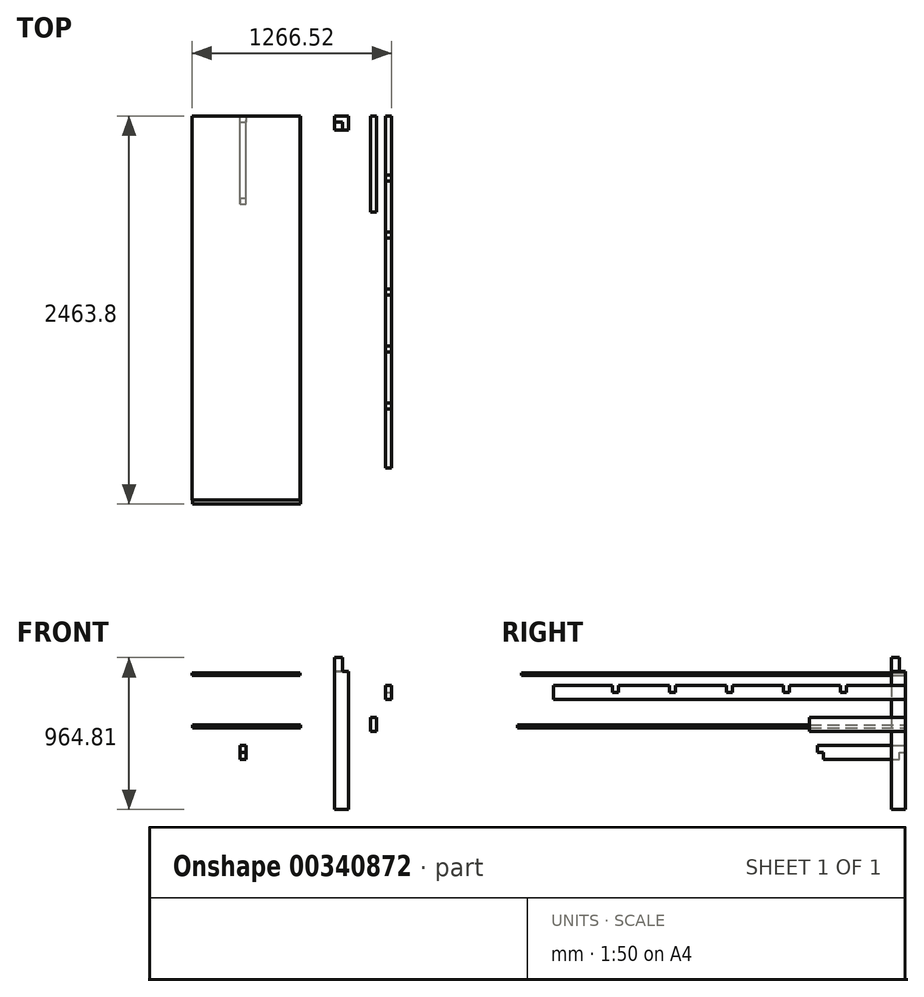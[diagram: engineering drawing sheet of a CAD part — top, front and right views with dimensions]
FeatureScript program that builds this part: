
annotation { "Feature Type Name" : "Feature", "Feature Type Description" : "" }
export const myFeature = defineFeature(function(context is Context, id is Id, definition is map)
    precondition{}
    {
        {
            var Q0;
            Q0=qCreatedBy(makeId("Front.planeOp"),FACE);
            var sketch = newSketch(context, id + "F0", { "sketchPlane" : qUnion([Q0])});
            skLineSegment(sketch, "E0.bottom", {"start": v(-17.05, 357.24) * mm, "end": v(-55.15, 357.24) * mm});
            skLineSegment(sketch, "E0.top", {"start": v(-17.05, -518.67) * mm, "end": v(-105.95, -518.67) * mm});
            skLineSegment(sketch, "E0.left", {"start": v(-17.05, 357.24) * mm, "end": v(-17.05, -518.67) * mm});
            skLineSegment(sketch, "E1", {"start": v(-105.95, -518.67) * mm, "end": v(-105.95, 446.14) * mm});
            skLineSegment(sketch, "E2", {"start": v(-105.95, 446.14) * mm, "end": v(-55.15, 446.14) * mm});
            skLineSegment(sketch, "E3", {"start": v(-55.15, 446.14) * mm, "end": v(-55.15, 357.24) * mm});
            skPoint(sketch, "E4.orphan", {"position": v(-105.95, 357.24) * mm});
            skLineSegment(sketch, "E5", {"start": v(-105.95, -518.67) * mm, "end": v(-105.95, 805.3) * mm, "construction": true});
            skPoint(sketch, "E6", {"position": v(-105.95, 805.3) * mm});
            skPoint(sketch, "E7", {"position": v(-105.95, 737.04) * mm});
            skPoint(sketch, "E8", {"position": v(-105.95, 678.3) * mm});
            skPoint(sketch, "E9", {"position": v(-105.95, 605.28) * mm});
            skPoint(sketch, "E10", {"position": v(-105.95, 464) * mm});
            skPoint(sketch, "E11", {"position": v(-105.95, 483.04) * mm});
            skSolve(sketch);
        }
        {
            var Q0;
            Q0=makeQuery(id+"F0.imprint","IMPRINT",FACE,{"disambiguationData":[TD([[makeQuery(id+"F0.imprint","IMPRINT",EDGE,{"derivedFrom":sQuery(id+"F0.wireOp",EDGE,"E0.bottom")}),1.0]])]});
            extrude(context, id + "F1", {"entities" : qUnion([Q0]), "depth" : 88.9 * mm, "offsetDistance" : 25.4 * mm});
        }
        {
            var Q0;
            Q0=makeQuery(id+"F1.opExtrude","SWEPT_FACE",FACE,{"disambiguationData":[OSD([sQuery(id+"F0.wireOp",EDGE,"E3")])]});
            var sketch = newSketch(context, id + "F2", { "sketchPlane" : qUnion([Q0])});
            skLineSegment(sketch, "E12.bottom", {"start": v(0, 446.14) * mm, "end": v(-38.1, 446.14) * mm});
            skLineSegment(sketch, "E12.top", {"start": v(0, 357.24) * mm, "end": v(-38.1, 357.24) * mm});
            skLineSegment(sketch, "E12.left", {"start": v(0, 446.14) * mm, "end": v(0, 357.24) * mm});
            skLineSegment(sketch, "E12.right", {"start": v(-38.1, 446.14) * mm, "end": v(-38.1, 357.24) * mm});
            skSolve(sketch);
        }
        {
            var Q0;
            Q0=makeQuery(id+"F2.imprint","IMPRINT",FACE,{"disambiguationData":[TD([[makeQuery(id+"F2.imprint","IMPRINT",EDGE,{"derivedFrom":sQuery(id+"F2.wireOp",EDGE,"E12.bottom")}),-1.0]])]});
            var Q1;
            Q1=makeQuery(id+"F1.opExtrude","SWEPT_FACE",FACE,{"disambiguationData":[OSD([sQuery(id+"F0.wireOp",EDGE,"E1")])]});
            extrude(context, id + "F3", {"entities" : qUnion([Q0]), "operationType" : NewBodyOperationType.REMOVE, "endBound" : BoundingType.UP_TO_SURFACE, "oppositeDirection" : true, "depth" : 25.4 * mm, "endBoundEntityFace" : qUnion([Q1]), "offsetDistance" : 25.4 * mm});
        }
        {
            var Q0;
            Q0=qCreatedBy(makeId("Front.planeOp"),FACE);
            var sketch = newSketch(context, id + "F4", { "sketchPlane" : qUnion([Q0])});
            skLineSegment(sketch, "E13.bottom", {"start": v(217.3, 269.52) * mm, "end": v(255.4, 269.52) * mm});
            skLineSegment(sketch, "E13.top", {"start": v(217.3, 180.62) * mm, "end": v(255.4, 180.62) * mm});
            skLineSegment(sketch, "E13.left", {"start": v(217.3, 269.52) * mm, "end": v(217.3, 180.62) * mm});
            skLineSegment(sketch, "E13.right", {"start": v(255.4, 269.52) * mm, "end": v(255.4, 180.62) * mm});
            skSolve(sketch);
        }
        {
            var Q0;
            Q0=makeQuery(id+"F4.imprint","IMPRINT",FACE,{"disambiguationData":[TD([[makeQuery(id+"F4.imprint","IMPRINT",EDGE,{"derivedFrom":sQuery(id+"F4.wireOp",EDGE,"E13.bottom")}),-1.0]])]});
            extrude(context, id + "F5", {"entities" : qUnion([Q0]), "depth" : 2235.2 * mm, "offsetDistance" : 25.4 * mm});
        }
        {
            var Q0;
            Q0=makeQuery(id+"F5.opExtrude","SWEPT_FACE",FACE,{"disambiguationData":[OSD([sQuery(id+"F4.wireOp",EDGE,"E13.right")])]});
            var sketch = newSketch(context, id + "F6", { "sketchPlane" : qUnion([Q0])});
            skLineSegment(sketch, "E14.bottom", {"start": v(-1136.65, 269.52) * mm, "end": v(-1098.55, 269.52) * mm});
            skLineSegment(sketch, "E14.top", {"start": v(-1136.65, 225.07) * mm, "end": v(-1098.55, 225.07) * mm});
            skLineSegment(sketch, "E14.left", {"start": v(-1136.65, 269.52) * mm, "end": v(-1136.65, 225.07) * mm});
            skLineSegment(sketch, "E14.right", {"start": v(-1098.55, 269.52) * mm, "end": v(-1098.55, 225.07) * mm});
            skPoint(sketch, "E15", {"position": v(-1117.6, 269.52) * mm});
            skLineSegment(sketch, "E16.1.0.0", {"start": v(-774.7, 269.52) * mm, "end": v(-736.6, 269.52) * mm});
            skLineSegment(sketch, "E16.1.0.1", {"start": v(-736.6, 269.52) * mm, "end": v(-736.6, 225.07) * mm});
            skLineSegment(sketch, "E16.1.0.2", {"start": v(-774.7, 225.07) * mm, "end": v(-736.6, 225.07) * mm});
            skLineSegment(sketch, "E16.1.0.3", {"start": v(-774.7, 269.52) * mm, "end": v(-774.7, 225.07) * mm});
            skLineSegment(sketch, "E16.2.0.0", {"start": v(-412.75, 269.52) * mm, "end": v(-374.65, 269.52) * mm});
            skLineSegment(sketch, "E16.2.0.1", {"start": v(-374.65, 269.52) * mm, "end": v(-374.65, 225.07) * mm});
            skLineSegment(sketch, "E16.2.0.2", {"start": v(-412.75, 225.07) * mm, "end": v(-374.65, 225.07) * mm});
            skLineSegment(sketch, "E16.2.0.3", {"start": v(-412.75, 269.52) * mm, "end": v(-412.75, 225.07) * mm});
            skLineSegment(sketch, "E16.direction1", {"start": v(-1136.65, 225.07) * mm, "end": v(-774.7, 225.07) * mm, "construction": true});
            skLineSegment(sketch, "E17", {"start": v(-1117.6, 269.52) * mm, "end": v(-1117.6, 180.62) * mm, "construction": true});
            skLineSegment(sketch, "E18.MirrorCS", {"start": v(-1098.55, 269.52) * mm, "end": v(-1136.65, 269.52) * mm});
            skLineSegment(sketch, "E19.MirrorCS", {"start": v(-1460.5, 269.52) * mm, "end": v(-1460.5, 225.07) * mm});
            skLineSegment(sketch, "E20.MirrorCS", {"start": v(-1498.6, 269.52) * mm, "end": v(-1498.6, 225.07) * mm});
            skLineSegment(sketch, "E21.MirrorCS", {"start": v(-1460.5, 269.52) * mm, "end": v(-1498.6, 269.52) * mm});
            skLineSegment(sketch, "E22.MirrorCS", {"start": v(-1460.5, 225.07) * mm, "end": v(-1498.6, 225.07) * mm});
            skLineSegment(sketch, "E23.MirrorCS", {"start": v(-1822.45, 269.52) * mm, "end": v(-1822.45, 225.07) * mm});
            skLineSegment(sketch, "E24.MirrorCS", {"start": v(-1822.45, 269.52) * mm, "end": v(-1860.55, 269.52) * mm});
            skLineSegment(sketch, "E25.MirrorCS", {"start": v(-1860.55, 269.52) * mm, "end": v(-1860.55, 225.07) * mm});
            skLineSegment(sketch, "E26.MirrorCS", {"start": v(-1822.45, 225.07) * mm, "end": v(-1860.55, 225.07) * mm});
            skSolve(sketch);
        }
        {
            var Q0;
            Q0=qCreatedBy(makeId("Front.planeOp"),FACE);
            var sketch = newSketch(context, id + "F7", { "sketchPlane" : qUnion([Q0])});
            skLineSegment(sketch, "E27.bottom", {"start": v(121.58, 66.17) * mm, "end": v(159.68, 66.17) * mm});
            skLineSegment(sketch, "E27.top", {"start": v(121.58, -22.73) * mm, "end": v(159.68, -22.73) * mm});
            skLineSegment(sketch, "E27.left", {"start": v(121.58, 66.17) * mm, "end": v(121.58, -22.73) * mm});
            skLineSegment(sketch, "E27.right", {"start": v(159.68, 66.17) * mm, "end": v(159.68, -22.73) * mm});
            skSolve(sketch);
        }
        {
            var Q0;
            Q0=makeQuery(id+"F7.imprint","IMPRINT",FACE,{"disambiguationData":[TD([[makeQuery(id+"F7.imprint","IMPRINT",EDGE,{"derivedFrom":sQuery(id+"F7.wireOp",EDGE,"E27.bottom")}),-1.0]])]});
            extrude(context, id + "F8", {"entities" : qUnion([Q0]), "depth" : 609.6 * mm, "offsetDistance" : 25.4 * mm});
        }
        {
            var Q0;
            Q0=qCreatedBy(makeId("Front.planeOp"),FACE);
            var sketch = newSketch(context, id + "F9", { "sketchPlane" : qUnion([Q0])});
            skLineSegment(sketch, "E28.bottom", {"start": v(-1007.47, 19.05) * mm, "end": v(-321.67, 19.05) * mm});
            skLineSegment(sketch, "E28.top", {"start": v(-1007.47, 0) * mm, "end": v(-321.67, 0) * mm});
            skLineSegment(sketch, "E28.left", {"start": v(-1007.47, 19.05) * mm, "end": v(-1007.47, 0) * mm});
            skLineSegment(sketch, "E28.right", {"start": v(-321.67, 19.05) * mm, "end": v(-321.67, 0) * mm});
            skSolve(sketch);
        }
        {
            var Q0;
            Q0=makeQuery(id+"F9.imprint","IMPRINT",FACE,{"disambiguationData":[TD([[makeQuery(id+"F9.imprint","IMPRINT",EDGE,{"derivedFrom":sQuery(id+"F9.wireOp",EDGE,"E28.bottom")}),-1.0]])]});
            extrude(context, id + "F10", {"entities" : qUnion([Q0]), "depth" : 2463.8 * mm, "offsetDistance" : 25.4 * mm});
        }
        {
            var Q0;
            Q0=makeQuery(id+"F6.imprint","IMPRINT",FACE,{"disambiguationData":[TD([[makeQuery(id+"F6.imprint","IMPRINT",EDGE,{"derivedFrom":sQuery(id+"F6.wireOp",EDGE,"E23.MirrorCS")}),-1.0]])]});
            var Q1;
            Q1=makeQuery(id+"F6.imprint","IMPRINT",FACE,{"disambiguationData":[TD([[makeQuery(id+"F6.imprint","IMPRINT",EDGE,{"derivedFrom":sQuery(id+"F6.wireOp",EDGE,"E19.MirrorCS")}),-1.0]])]});
            var Q2;
            Q2=makeQuery(id+"F6.imprint","IMPRINT",FACE,{"disambiguationData":[TD([[makeQuery(id+"F6.imprint","IMPRINT",EDGE,{"derivedFrom":sQuery(id+"F6.wireOp",EDGE,"E14.top")}),1.0]])]});
            var Q3;
            Q3=makeQuery(id+"F6.imprint","IMPRINT",FACE,{"disambiguationData":[TD([[makeQuery(id+"F6.imprint","IMPRINT",EDGE,{"derivedFrom":sQuery(id+"F6.wireOp",EDGE,"E16.1.0.0")}),-1.0]])]});
            var Q4;
            Q4=makeQuery(id+"F6.imprint","IMPRINT",FACE,{"disambiguationData":[TD([[makeQuery(id+"F6.imprint","IMPRINT",EDGE,{"derivedFrom":sQuery(id+"F6.wireOp",EDGE,"E16.2.0.0")}),-1.0]])]});
            var Q5;
            Q5=makeQuery(id+"F5.opExtrude","SWEPT_FACE",FACE,{"disambiguationData":[OSD([sQuery(id+"F4.wireOp",EDGE,"E13.left")])]});
            var Q6;
            Q6=makeQuery(id+"F5.opExtrude","SWEPT_FACE",FACE,{"disambiguationData":[OSD([sQuery(id+"F4.wireOp",EDGE,"E13.left")])]});
            var Q7;
            Q7=makeQuery(id+"F5.opExtrude","SWEPT_FACE",FACE,{"disambiguationData":[OSD([sQuery(id+"F4.wireOp",EDGE,"E13.left")])]});
            extrude(context, id + "F11", {"entities" : qUnion([Q0, Q1, Q2, Q3, Q4]), "operationType" : NewBodyOperationType.REMOVE, "endBound" : BoundingType.UP_TO_SURFACE, "oppositeDirection" : true, "depth" : 25.4 * mm, "endBoundEntityFace" : qUnion([Q5, Q6, Q7]), "offsetDistance" : 25.4 * mm});
        }
        {
            var Q0;
            Q0=qCreatedBy(makeId("Front.planeOp"),FACE);
            var sketch = newSketch(context, id + "F12", { "sketchPlane" : qUnion([Q0])});
            skLineSegment(sketch, "E29.bottom", {"start": v(-707.68, -112.54) * mm, "end": v(-669.58, -112.54) * mm});
            skLineSegment(sketch, "E29.top", {"start": v(-707.68, -201.44) * mm, "end": v(-669.58, -201.44) * mm});
            skLineSegment(sketch, "E29.left", {"start": v(-707.68, -112.54) * mm, "end": v(-707.68, -201.44) * mm});
            skLineSegment(sketch, "E29.right", {"start": v(-669.58, -112.54) * mm, "end": v(-669.58, -201.44) * mm});
            skSolve(sketch);
        }
        {
            var Q0;
            Q0=makeQuery(id+"F12.imprint","IMPRINT",FACE,{"disambiguationData":[TD([[makeQuery(id+"F12.imprint","IMPRINT",EDGE,{"derivedFrom":sQuery(id+"F12.wireOp",EDGE,"E29.bottom")}),-1.0]])]});
            extrude(context, id + "F13", {"entities" : qUnion([Q0]), "depth" : 558.8 * mm, "offsetDistance" : 25.4 * mm});
        }
        {
            var Q0;
            Q0=makeQuery(id+"F13.opExtrude","SWEPT_FACE",FACE,{"disambiguationData":[OSD([sQuery(id+"F12.wireOp",EDGE,"E29.right")])]});
            var sketch = newSketch(context, id + "F14", { "sketchPlane" : qUnion([Q0])});
            skLineSegment(sketch, "E30", {"start": v(-279.4, -112.54) * mm, "end": v(-279.4, -201.44) * mm, "construction": true});
            skLineSegment(sketch, "E31", {"start": v(-558.8, -156.99) * mm, "end": v(-520.7, -156.99) * mm});
            skLineSegment(sketch, "E32", {"start": v(-520.7, -156.99) * mm, "end": v(-520.7, -201.44) * mm});
            skLineSegment(sketch, "E33.MirrorCS", {"start": v(0, -156.99) * mm, "end": v(-38.1, -156.99) * mm});
            skLineSegment(sketch, "E34.MirrorCS", {"start": v(-38.1, -156.99) * mm, "end": v(-38.1, -201.44) * mm});
            skSolve(sketch);
        }
        {
            var Q0;
            {var subQ0=sQuery(id+"F14.wireOp",EDGE,"E31");Q0=makeQuery(id+"F14.imprint","IMPRINT",FACE,{"disambiguationData":[TD([[makeQuery(id+"F14.imprint","IMPRINT",EDGE,{"derivedFrom":subQ0}),-1.0]])]});}
            var Q1;
            {var subQ0=sQuery(id+"F14.wireOp",EDGE,"E33.MirrorCS");Q1=makeQuery(id+"F14.imprint","IMPRINT",FACE,{"disambiguationData":[TD([[makeQuery(id+"F14.imprint","IMPRINT",EDGE,{"derivedFrom":subQ0}),1.0]])]});}
            extrude(context, id + "F15", {"entities" : qUnion([Q0, Q1]), "operationType" : NewBodyOperationType.REMOVE, "endBound" : BoundingType.UP_TO_NEXT, "oppositeDirection" : true, "depth" : 25.4 * mm, "offsetDistance" : 25.4 * mm});
        }
        {
            var Q0;
            Q0=qCreatedBy(makeId("Front.planeOp"),FACE);
            var sketch = newSketch(context, id + "F16", { "sketchPlane" : qUnion([Q0])});
            skLineSegment(sketch, "E35.bottom", {"start": v(-1011.13, 348.62) * mm, "end": v(-325.33, 348.62) * mm});
            skLineSegment(sketch, "E35.top", {"start": v(-1011.13, 330.76) * mm, "end": v(-325.33, 330.76) * mm});
            skLineSegment(sketch, "E35.left", {"start": v(-1011.13, 348.62) * mm, "end": v(-1011.13, 330.76) * mm});
            skLineSegment(sketch, "E35.right", {"start": v(-325.33, 348.62) * mm, "end": v(-325.33, 330.76) * mm});
            skSolve(sketch);
        }
        {
            var Q0;
            Q0=makeQuery(id+"F16.imprint","IMPRINT",FACE,{"disambiguationData":[TD([[makeQuery(id+"F16.imprint","IMPRINT",EDGE,{"derivedFrom":sQuery(id+"F16.wireOp",EDGE,"E35.bottom")}),-1.0]])]});
            extrude(context, id + "F17", {"entities" : qUnion([Q0]), "depth" : 2438.4 * mm, "offsetDistance" : 25.4 * mm});
        }
    });
